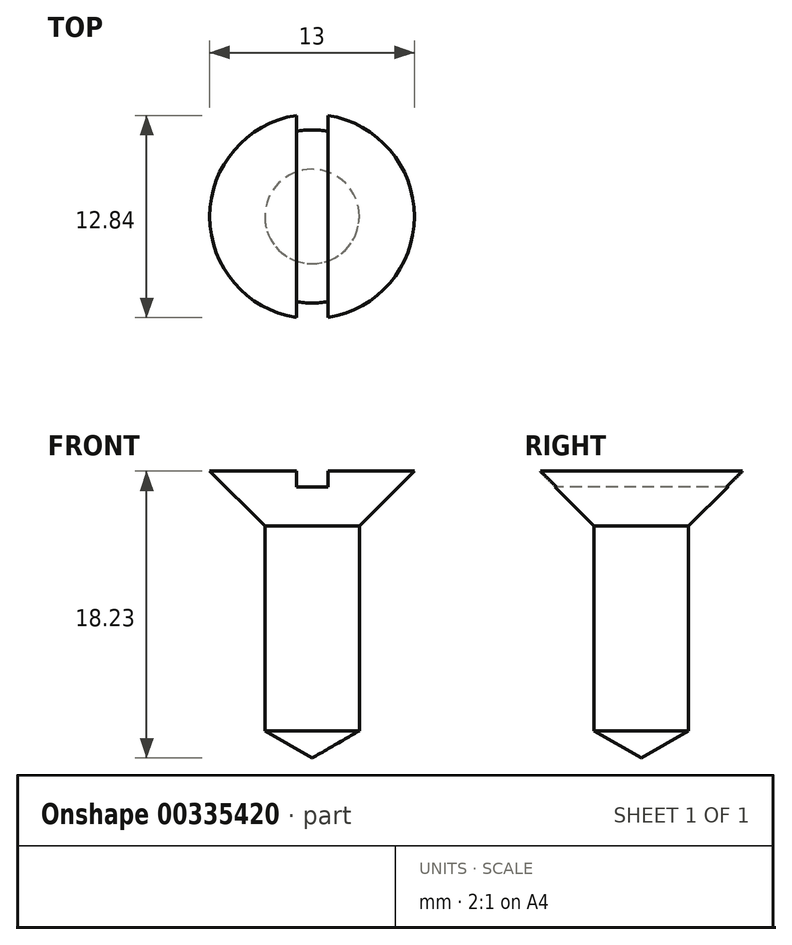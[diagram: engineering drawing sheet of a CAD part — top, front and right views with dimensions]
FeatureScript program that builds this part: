
annotation { "Feature Type Name" : "Feature", "Feature Type Description" : "" }
export const myFeature = defineFeature(function(context is Context, id is Id, definition is map)
    precondition{}
    {
        {
            var Q0;
            Q0=qCreatedBy(makeId("Top.planeOp"),FACE);
            var sketch = newSketch(context, id + "F0", { "sketchPlane" : qUnion([Q0])});
            skCircle(sketch, "E0", {"center": v(0, 0) * mm, "radius": 3 * mm});
            skSolve(sketch);
        }
        {
            var Q0;
            Q0=makeQuery(id+"F0.imprint","IMPRINT",FACE,{"disambiguationData":[TD([[makeQuery(id+"F0.imprint","IMPRINT",EDGE,{"derivedFrom":sQuery(id+"F0.wireOp",EDGE,"E0")}),1.0]])]});
            extrude(context, id + "F1", {"entities" : qUnion([Q0]), "depth" : 13 * mm});
        }
        {
            var Q0;
            Q0=qCreatedBy(makeId("Front.planeOp"),FACE);
            var sketch = newSketch(context, id + "F2", { "sketchPlane" : qUnion([Q0])});
            skLineSegment(sketch, "E1", {"start": v(0, 0) * mm, "end": v(0, -5.31) * mm});
            skLineSegment(sketch, "E2", {"start": v(0, 0) * mm, "end": v(3, 0) * mm});
            skLineSegment(sketch, "E3", {"start": v(3, 0) * mm, "end": v(0, -1.73) * mm});
            skLineSegment(sketch, "E4", {"start": v(0, -1.73) * mm, "end": v(0, 0) * mm});
            skSolve(sketch);
        }
        {
            var Q0;
            Q0=makeQuery(id+"F2.imprint","IMPRINT",FACE,{"disambiguationData":[TD([[makeQuery(id+"F2.imprint","IMPRINT",EDGE,{"derivedFrom":sQuery(id+"F2.wireOp",EDGE,"E2")}),-1.0]])]});
            var Q1;
            Q1=sQuery(id+"F2.wireOp",EDGE,"E4");
            revolve(context, id + "F3", {"entities" : qUnion([Q0]), "axis" : qUnion([Q1]), "revolveType" : RevolveType.FULL});
        }
        {
            var Q0;
            Q0=qCreatedBy(makeId("Front.planeOp"),FACE);
            var sketch = newSketch(context, id + "F4", { "sketchPlane" : qUnion([Q0])});
            skLineSegment(sketch, "E5", {"start": v(0, 0) * mm, "end": v(0, 13) * mm});
            skLineSegment(sketch, "E6", {"start": v(0, 13) * mm, "end": v(-3, 13) * mm});
            skLineSegment(sketch, "E7", {"start": v(-3, 13) * mm, "end": v(-6.5, 16.5) * mm});
            skLineSegment(sketch, "E8", {"start": v(-1, 16.5) * mm, "end": v(-6.5, 16.5) * mm});
            skLineSegment(sketch, "E9", {"start": v(0, 13) * mm, "end": v(0, 15.5) * mm});
            skLineSegment(sketch, "E10", {"start": v(-1, 16.5) * mm, "end": v(0, 16.5) * mm});
            skLineSegment(sketch, "E11", {"start": v(0, 15.5) * mm, "end": v(0, 16.5) * mm});
            skSolve(sketch);
        }
        {
            var Q0;
            {var subQ2=sQuery(id+"F4.wireOp",EDGE,"E6");Q0=makeQuery(id+"F4.imprint","IMPRINT",FACE,{"disambiguationData":[TD([[makeQuery(id+"F4.imprint","IMPRINT",EDGE,{"derivedFrom":subQ2}),-1.0]])]});}
            var Q1;
            Q1=sQuery(id+"F4.wireOp",EDGE,"E9");
            revolve(context, id + "F5", {"operationType" : NewBodyOperationType.ADD, "entities" : qUnion([Q0]), "axis" : qUnion([Q1]), "revolveType" : RevolveType.FULL});
        }
        {
            var Q0;
            Q0=qCreatedBy(makeId("Front.planeOp"),FACE);
            var sketch = newSketch(context, id + "F6", { "sketchPlane" : qUnion([Q0])});
            skLineSegment(sketch, "E12", {"start": v(0, 0) * mm, "end": v(0, 15.5) * mm});
            skLineSegment(sketch, "E13", {"start": v(0, 15.5) * mm, "end": v(-1, 15.5) * mm});
            skLineSegment(sketch, "E14", {"start": v(-1, 15.5) * mm, "end": v(-1, 16.5) * mm});
            skLineSegment(sketch, "E15.MirrorCS", {"start": v(-2, 15.5) * mm, "end": v(-1, 15.5) * mm});
            skLineSegment(sketch, "E16", {"start": v(0, 15.5) * mm, "end": v(1, 15.5) * mm});
            skLineSegment(sketch, "E17", {"start": v(1, 15.5) * mm, "end": v(1, 16.5) * mm});
            skLineSegment(sketch, "E18", {"start": v(-1, 16.5) * mm, "end": v(1, 16.5) * mm});
            skSolve(sketch);
        }
        {
            var Q0;
            Q0 = qSketchRegion(id + "F6", true);
            extrude(context, id + "F7", {"entities" : qUnion([Q0]), "operationType" : NewBodyOperationType.REMOVE, "endBound" : BoundingType.SYMMETRIC, "oppositeDirection" : true, "depth" : 25 * mm});
        }
    });
